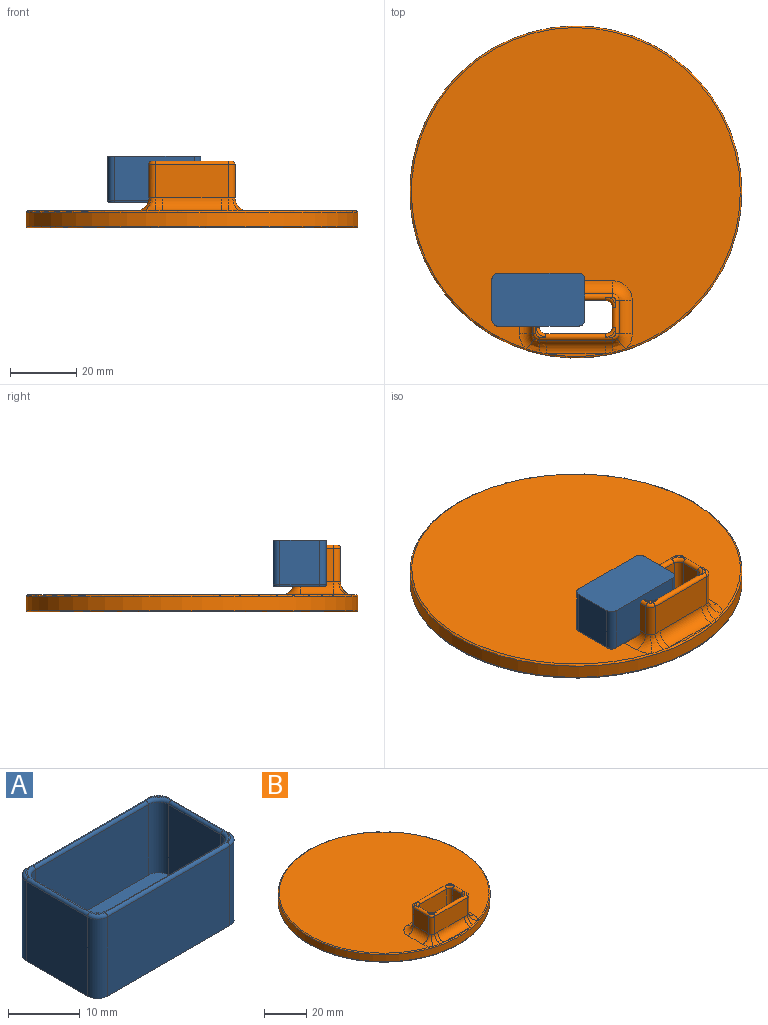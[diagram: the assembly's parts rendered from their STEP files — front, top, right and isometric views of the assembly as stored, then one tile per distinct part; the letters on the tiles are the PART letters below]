
ASSEMBLY  parts=2 mates=1
PART A: 38 faces, bbox 28.4x16.4x14 mm
  f0: plane 1.7x1.7mm, normal (0,0,1), area 0.5mm2, adj f22,f26,f27,f31
  f1: plane 1.7x1.7mm, normal (0,0,1), area 0.5mm2, adj f31,f32,f36,f37
  f2: plane 1.7x1.7mm, normal (0,0,1), area 0.5mm2, adj f22,f24,f25,f30
  f3: plane 13.5x12mm, normal (1,0,0), area 162mm2, adj f4,f10,f11,f30
  f4: cylinder r=2mm len=13.5mm, axis (0,0,-1), area 42.4mm2, adj f3,f5,f11,f25
  f5: plane 24x13.5mm, normal (0,1,0), area 324mm2, adj f4,f6,f11,f22
  f6: cylinder r=2mm len=13.5mm, axis (0,0,-1), area 42.4mm2, adj f5,f7,f11,f26
  f7: plane 13.5x12mm, normal (-1,0,0), area 162mm2, adj f6,f8,f11,f31
  f8: cylinder r=2mm len=13.5mm, axis (0,0,-1), area 42.4mm2, adj f7,f9,f11,f36
  f9: plane 24x13.5mm, normal (0,-1,0), area 324mm2, adj f8,f10,f11,f37
  f10: cylinder r=2mm len=13.5mm, axis (0,0,-1), area 42.4mm2, adj f3,f9,f11,f35
  f11: plane 28x16mm, normal (0,0,-1), area 444.6mm2, adj f3,f4,f5,f6,f7,f8,f9,f10
  f12: cylinder r=2mm len=12mm, axis (0,0,-1), area 37.7mm2, adj f13,f19,f21,f24
  f13: plane 12x10.2mm, normal (-1,0,0), area 122.4mm2, adj f12,f14,f21,f29
  f14: cylinder r=2mm len=12mm, axis (0,0,-1), area 37.7mm2, adj f13,f15,f21,f34
  f15: plane 22.2x12mm, normal (0,1,0), area 266.4mm2, adj f14,f16,f21,f33
  f16: cylinder r=2mm len=12mm, axis (0,0,-1), area 37.7mm2, adj f15,f17,f21,f32
  f17: plane 12x10.2mm, normal (1,0,0), area 122.4mm2, adj f16,f18,f21,f28
  f18: cylinder r=2mm len=12mm, axis (0,0,-1), area 37.7mm2, adj f17,f19,f21,f27
  f19: plane 22.2x12mm, normal (0,-1,0), area 266.4mm2, adj f12,f18,f21,f23
  f20: plane 1.7x1.7mm, normal (0,0,1), area 0.5mm2, adj f30,f34,f35,f37
  f21: plane 26.2x14.2mm, normal (0,0,1), area 368.6mm2, adj f12,f13,f14,f15,f16,f17,f18,f19
  f22: cylinder r=0.5mm len=24mm, axis (1,0,0), area 17.7mm2, adj f0,f2,f5,f23,f24,f25,f26,f27
  f23: cylinder r=0.5mm len=22.2mm, axis (-1,0,0), area 16.3mm2, adj f19,f22,f24,f27
  f24: torus R=2.5mm, axis (0,0,1), area 2.6mm2, adj f2,f12,f22,f23,f29,f30
  f25: torus R=1.5mm, axis (0,0,1), area 2.2mm2, adj f2,f4,f22,f30
  f26: torus R=1.5mm, axis (0,0,1), area 2.2mm2, adj f0,f6,f22,f31
  f27: torus R=2.5mm, axis (0,0,1), area 2.6mm2, adj f0,f18,f22,f23,f28,f31
  f28: cylinder r=0.5mm len=10.2mm, axis (0,-1,0), area 7.5mm2, adj f17,f27,f31,f32
  f29: cylinder r=0.5mm len=10.2mm, axis (0,1,0), area 7.5mm2, adj f13,f24,f30,f34
  f30: cylinder r=0.5mm len=12mm, axis (0,-1,0), area 8.9mm2, adj f2,f3,f20,f24,f25,f29,f34,f35
  f31: cylinder r=0.5mm len=12mm, axis (0,1,0), area 8.9mm2, adj f0,f1,f7,f26,f27,f28,f32,f36
  f32: torus R=2.5mm, axis (0,0,1), area 2.6mm2, adj f1,f16,f28,f31,f33,f37
  f33: cylinder r=0.5mm len=22.2mm, axis (1,0,0), area 16.3mm2, adj f15,f32,f34,f37
  f34: torus R=2.5mm, axis (0,0,1), area 2.6mm2, adj f14,f20,f29,f30,f33,f37
  f35: torus R=1.5mm, axis (0,0,1), area 2.2mm2, adj f10,f20,f30,f37
  f36: torus R=1.5mm, axis (0,0,1), area 2.2mm2, adj f1,f8,f31,f37
  f37: cylinder r=0.5mm len=24mm, axis (-1,0,0), area 17.7mm2, adj f1,f9,f20,f32,f33,f34,f35,f36
PART B: 56 faces, bbox 108.2x108.2x20.1 mm
  f0: plane 3x3mm, normal (0,0,1), area 1.7mm2, adj f44,f46,f49,f50
  f1: plane 3x3mm, normal (0,0,1), area 1.7mm2, adj f50,f51,f53,f55
  f2: plane 3x3mm, normal (0,0,1), area 1.7mm2, adj f44,f45,f47,f48
  f3: plane 17.76x0.8mm, normal (0,0,1), area 9.5mm2, adj f10,f35
  f4: plane 95x95mm, normal (0,0,1), area 440.6mm2, adj f5,f14
  f5: torus R=47.5mm, axis (0,0,1), area 236mm2, adj f4,f6
  f6: cylinder r=48mm len=96mm, axis (0,0,1), area 512.7mm2, adj f5,f7
  f7: torus R=47.5mm, axis (0,0,1), area 236mm2, adj f6,f8
  f8: plane 95x95mm, normal (0,0,-1), area 6871.7mm2, adj f7,f15,f16,f17,f18,f19,f20,f21
  f9: plane 99x96.67mm, normal (0,0,1), area 6975.7mm2, adj f10,f34,f36,f38,f40,f41,f42,f43
  f10: torus R=49.5mm, axis (0,0,1), area 245.3mm2, adj f3,f9,f11,f32,f33,f37,f39
  f11: cylinder r=50mm len=100mm, axis (0,0,1), area 1288.1mm2, adj f10,f12
  f12: torus R=49.5mm, axis (0,0,1), area 245.8mm2, adj f11,f13
  f13: plane 99x99mm, normal (0,0,-1), area 1050.1mm2, adj f12,f14
  f14: torus R=46mm, axis (0,0,1), area 450.9mm2, adj f4,f13
  f15: plane 15.4x6mm, normal (-1,0,0), area 92.4mm2, adj f8,f16,f22,f47
  f16: cylinder r=2mm len=15.4mm, axis (0,0,1), area 48.4mm2, adj f8,f15,f17,f45
  f17: plane 18x15.4mm, normal (0,-1,0), area 277.2mm2, adj f8,f16,f18,f44
  f18: cylinder r=2mm len=15.4mm, axis (0,0,1), area 48.4mm2, adj f8,f17,f19,f46
  f19: plane 15.4x6mm, normal (1,0,0), area 92.4mm2, adj f8,f18,f20,f50
  f20: cylinder r=2mm len=15.4mm, axis (0,0,1), area 48.4mm2, adj f8,f19,f21,f51
  f21: plane 18x15.4mm, normal (0,1,0), area 277.2mm2, adj f8,f20,f22,f53
  f22: cylinder r=2mm len=15.4mm, axis (0,0,1), area 48.4mm2, adj f8,f15,f21,f52
  f23: plane 10x10mm, normal (1,0,0), area 100mm2, adj f24,f30,f43,f47
  f24: cylinder r=2mm len=10mm, axis (0,0,-1), area 31.4mm2, adj f23,f25,f42,f48
  f25: plane 22x10mm, normal (0,1,0), area 220mm2, adj f24,f26,f40,f44
  f26: cylinder r=2mm len=10mm, axis (0,0,-1), area 31.4mm2, adj f25,f27,f38,f49
  f27: plane 10x10mm, normal (-1,0,0), area 100mm2, adj f26,f28,f36,f50
  f28: cylinder r=2mm len=10.02mm, axis (0,0,-1), area 31.4mm2, adj f27,f29,f32,f34,f55
  f29: plane 22x10.02mm, normal (0,-1,0), area 220mm2, adj f28,f30,f33,f35,f37,f53
  f30: cylinder r=2mm len=10.02mm, axis (0,0,-1), area 31.4mm2, adj f23,f29,f39,f41,f54
  f31: plane 3x3mm, normal (0,0,1), area 1.7mm2, adj f47,f52,f53,f54
  f32: bspline ~5.87x4.52mm, area 14.4mm2, adj f10,f28,f33,f34
  f33: bspline ~6.37x4.31mm, area 12.6mm2, adj f10,f29,f32,f35
  f34: torus R=6mm, axis (0,0,-1), area 18.3mm2, adj f9,f28,f32,f36
  f35: cylinder r=4mm len=17.76mm, axis (-1,0,0), area 111.6mm2, adj f3,f29,f33,f37
  f36: cylinder r=4mm len=10mm, axis (0,1,0), area 62.8mm2, adj f9,f27,f34,f38
  f37: bspline ~8x4.66mm, area 12.6mm2, adj f10,f29,f35,f39
  f38: torus R=6mm, axis (0,0,-1), area 34.1mm2, adj f9,f26,f36,f40
  f39: bspline ~5.78x4.57mm, area 14.4mm2, adj f10,f30,f37,f41
  f40: cylinder r=4mm len=22mm, axis (1,0,0), area 138.2mm2, adj f9,f25,f38,f42
  f41: torus R=6mm, axis (0,0,-1), area 18.3mm2, adj f9,f30,f39,f43
  f42: torus R=6mm, axis (0,0,-1), area 34.1mm2, adj f9,f24,f40,f43
  f43: cylinder r=4mm len=10mm, axis (0,-1,0), area 62.8mm2, adj f9,f23,f41,f42
  f44: cylinder r=1mm len=22mm, axis (1,0,0), area 62.8mm2, adj f0,f2,f17,f25,f45,f46,f48,f49
  f45: torus R=3mm, axis (0,0,1), area 5.8mm2, adj f2,f16,f44,f47
  f46: torus R=3mm, axis (0,0,1), area 5.8mm2, adj f0,f18,f44,f50
  f47: cylinder r=1mm len=10mm, axis (0,-1,0), area 25.1mm2, adj f2,f15,f23,f31,f45,f48,f52,f54
  f48: torus R=1mm, axis (0,0,1), area 4mm2, adj f2,f24,f44,f47
  f49: torus R=1mm, axis (0,0,1), area 4mm2, adj f0,f26,f44,f50
  f50: cylinder r=1mm len=10mm, axis (0,1,0), area 25.1mm2, adj f0,f1,f19,f27,f46,f49,f51,f55
  f51: torus R=3mm, axis (0,0,1), area 5.8mm2, adj f1,f20,f50,f53
  f52: torus R=3mm, axis (0,0,1), area 5.8mm2, adj f22,f31,f47,f53
  f53: cylinder r=1mm len=22mm, axis (-1,0,0), area 62.8mm2, adj f1,f21,f29,f31,f51,f52,f54,f55
  f54: torus R=1mm, axis (0,0,1), area 4mm2, adj f30,f31,f47,f53
  f55: torus R=1mm, axis (0,0,1), area 4mm2, adj f1,f28,f50,f53
PLACE A rot(axis=(1,0,0),180deg) t=(-34.33,-29.51,39.67)mm
PLACE B t=(-22.06,3.01,6.45)mm
MATE fastened A.f21 <-> B.f0  axis (0,0,-1) through (-33.33,-29.41,38.17)mm
